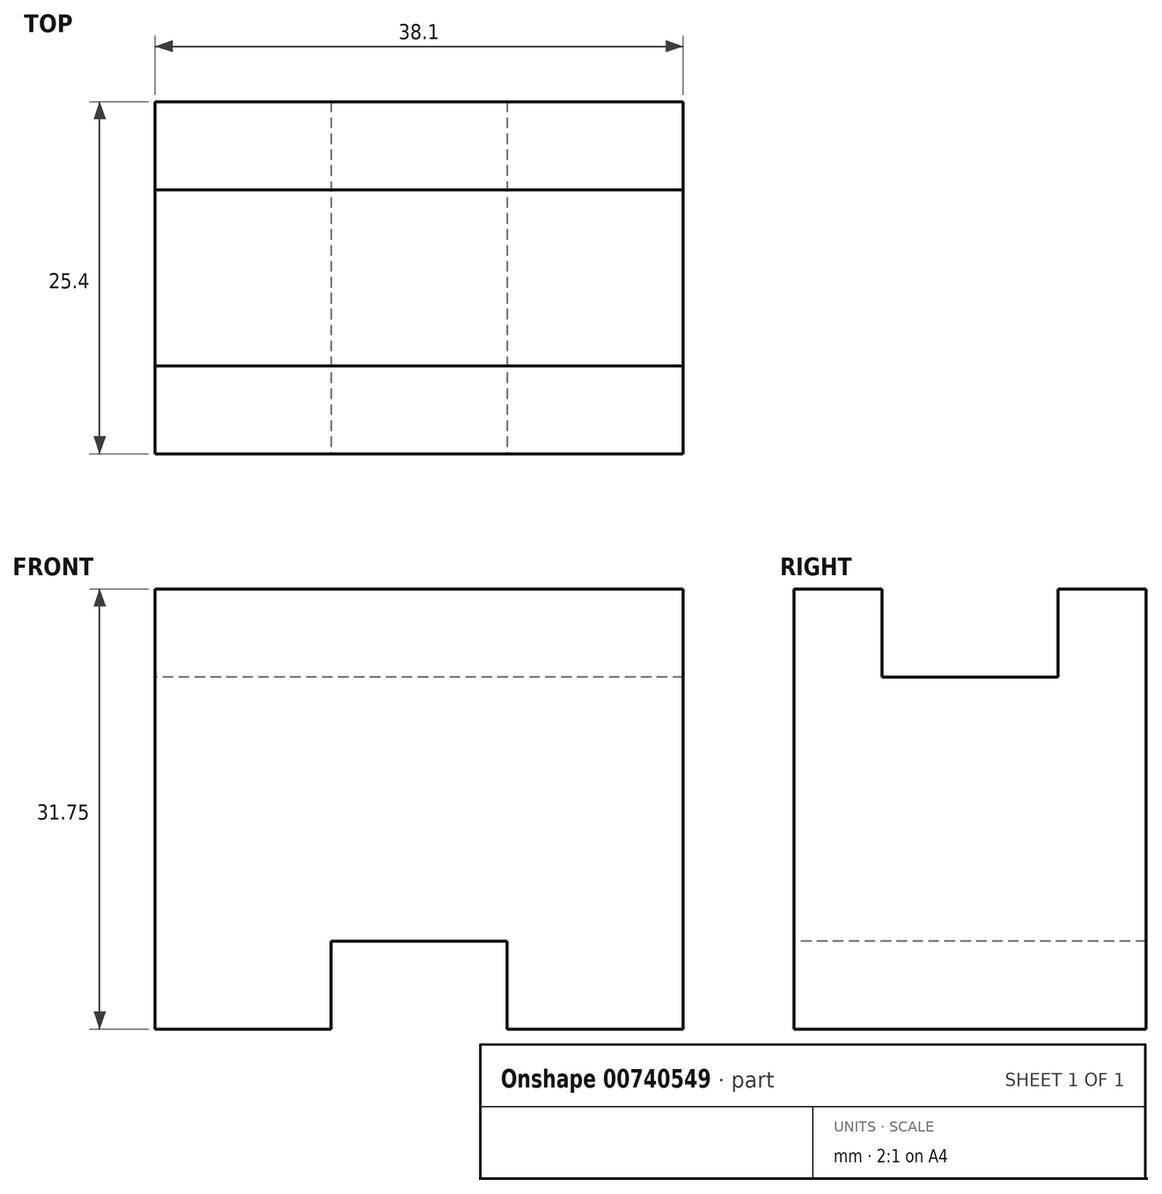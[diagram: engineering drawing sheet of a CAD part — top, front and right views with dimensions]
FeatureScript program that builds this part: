
annotation { "Feature Type Name" : "Feature", "Feature Type Description" : "" }
export const myFeature = defineFeature(function(context is Context, id is Id, definition is map)
    precondition{}
    {
        {
            var Q0;
            Q0=qCreatedBy(makeId("Right.planeOp"),FACE);
            var sketch = newSketch(context, id + "F0", { "sketchPlane" : qUnion([Q0])});
            skLineSegment(sketch, "E0", {"start": v(0, 0) * mm, "end": v(0, 31.75) * mm});
            skLineSegment(sketch, "E1", {"start": v(0, 31.75) * mm, "end": v(6.35, 31.75) * mm});
            skLineSegment(sketch, "E2", {"start": v(6.35, 31.75) * mm, "end": v(6.35, 25.4) * mm});
            skLineSegment(sketch, "E3", {"start": v(6.35, 25.4) * mm, "end": v(19.05, 25.4) * mm});
            skLineSegment(sketch, "E4", {"start": v(19.05, 25.4) * mm, "end": v(19.05, 31.75) * mm});
            skLineSegment(sketch, "E5", {"start": v(19.05, 31.75) * mm, "end": v(25.4, 31.75) * mm});
            skLineSegment(sketch, "E6", {"start": v(25.4, 31.75) * mm, "end": v(25.4, 0) * mm});
            skLineSegment(sketch, "E7", {"start": v(25.4, 0) * mm, "end": v(0, 0) * mm});
            skSolve(sketch);
        }
        {
            var Q0;
            Q0 = qSketchRegion(id + "F0", true);
            extrude(context, id + "F1", {"entities" : qUnion([Q0]), "depth" : 38.1 * mm, "offsetDistance" : 25.4 * mm});
        }
        {
            var Q0;
            Q0=makeQuery(id+"F1.opExtrude","SWEPT_FACE",FACE,{"disambiguationData":[OSD([sQuery(id+"F0.wireOp",EDGE,"E0")])]});
            var sketch = newSketch(context, id + "F2", { "sketchPlane" : qUnion([Q0])});
            skLineSegment(sketch, "E8", {"start": v(12.7, 0) * mm, "end": v(12.7, 6.35) * mm});
            skLineSegment(sketch, "E9", {"start": v(12.7, 6.35) * mm, "end": v(25.4, 6.35) * mm});
            skLineSegment(sketch, "E10", {"start": v(25.4, 6.35) * mm, "end": v(25.4, 0) * mm});
            skLineSegment(sketch, "E11", {"start": v(12.7, 0) * mm, "end": v(0, 0) * mm});
            skSolve(sketch);
        }
        {
            var Q0;
            Q0 = qSketchRegion(id + "F2", true);
            var Q1;
            {var subQ0=sQuery(id+"F2.wireOp",EDGE,"E8");Q1=makeQuery(id+"F2.imprint","IMPRINT",FACE,{"disambiguationData":[TD([[makeQuery(id+"F2.imprint","IMPRINT",EDGE,{"derivedFrom":subQ0}),-1.0]])]});}
            extrude(context, id + "F3", {"entities" : qUnion([Q0, Q1]), "operationType" : NewBodyOperationType.REMOVE, "endBound" : BoundingType.THROUGH_ALL, "oppositeDirection" : true, "depth" : 25.4 * mm, "offsetDistance" : 25.4 * mm});
        }
    });
